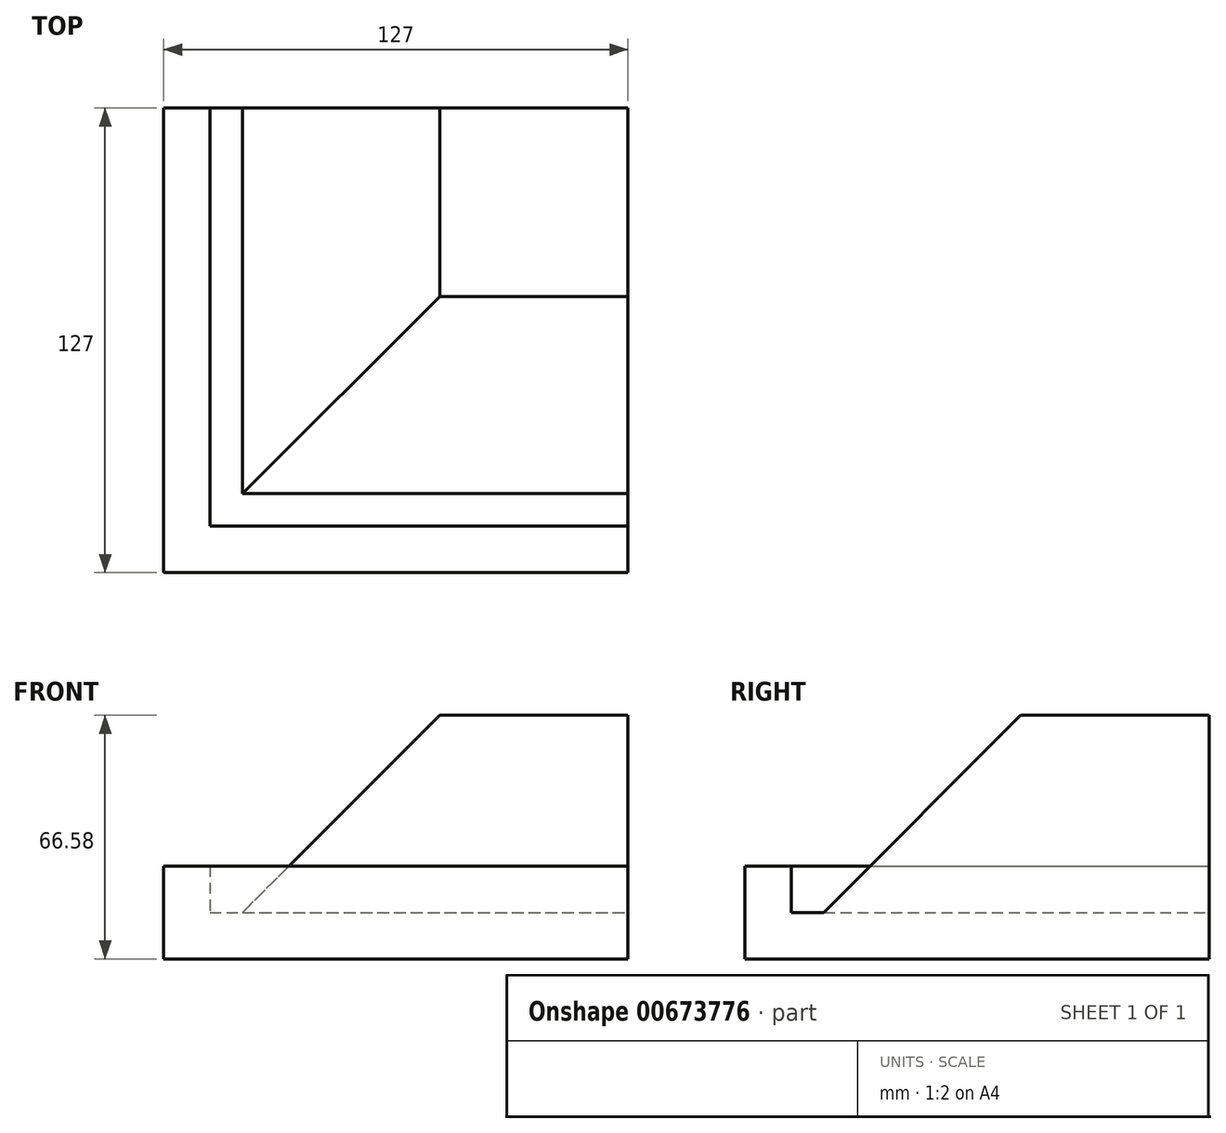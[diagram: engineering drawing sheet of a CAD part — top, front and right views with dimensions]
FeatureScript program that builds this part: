
annotation { "Feature Type Name" : "Feature", "Feature Type Description" : "" }
export const myFeature = defineFeature(function(context is Context, id is Id, definition is map)
    precondition{}
    {
        {
            var Q0;
            Q0=qCreatedBy(makeId("Top.planeOp"),FACE);
            var sketch = newSketch(context, id + "F0", { "sketchPlane" : qUnion([Q0])});
            skLineSegment(sketch, "E0.bottom", {"start": v(88.9, 88.9) * mm, "end": v(-88.9, 88.9) * mm});
            skLineSegment(sketch, "E0.top", {"start": v(88.9, -88.9) * mm, "end": v(-88.9, -88.9) * mm});
            skLineSegment(sketch, "E0.left", {"start": v(88.9, 88.9) * mm, "end": v(88.9, -88.9) * mm});
            skLineSegment(sketch, "E0.right", {"start": v(-88.9, 88.9) * mm, "end": v(-88.9, -88.9) * mm});
            skPoint(sketch, "E0.middle", {"position": v(0, 0) * mm});
            skSolve(sketch);
        }
        {
            var Q0;
            Q0 = qSketchRegion(id + "F0", true);
            extrude(context, id + "F1", {"entities" : qUnion([Q0]), "depth" : 76.2 * mm, "offsetDistance" : 25.4 * mm});
        }
        {
            var Q0;
            Q0=makeQuery(id+"F1.opExtrude","SWEPT_FACE",FACE,{"disambiguationData":[OSD([sQuery(id+"F0.wireOp",EDGE,"E0.bottom")])]});
            var sketch = newSketch(context, id + "F2", { "sketchPlane" : qUnion([Q0])});
            skLineSegment(sketch, "E1", {"start": v(88.9, 25.4) * mm, "end": v(76.2, 25.4) * mm});
            skLineSegment(sketch, "E2", {"start": v(76.2, 25.4) * mm, "end": v(76.2, 12.7) * mm});
            skLineSegment(sketch, "E3", {"start": v(76.2, 12.7) * mm, "end": v(67.31, 12.7) * mm});
            skLineSegment(sketch, "E4", {"start": v(67.31, 12.7) * mm, "end": v(13.43, 66.58) * mm});
            skLineSegment(sketch, "E5.0", {"start": v(-88.9, 0) * mm, "end": v(88.9, 0) * mm});
            skLineSegment(sketch, "E6", {"start": v(13.43, 66.58) * mm, "end": v(-11.97, 66.58) * mm});
            skLineSegment(sketch, "E7", {"start": v(-11.97, 66.58) * mm, "end": v(-11.97, 0) * mm});
            skLineSegment(sketch, "E8", {"start": v(-11.97, 66.58) * mm, "end": v(-11.97, 76.2) * mm});
            skLineSegment(sketch, "E9", {"start": v(-38.1, 0) * mm, "end": v(-38.1, 76.2) * mm});
            skSolve(sketch);
        }
        {
            var Q0;
            {var subQ5=sQuery(id+"F2.wireOp",EDGE,"E1");Q0=makeQuery(id+"F2.imprint","IMPRINT",FACE,{"disambiguationData":[TD([[makeQuery(id+"F2.imprint","IMPRINT",EDGE,{"derivedFrom":subQ5}),-1.0]])]});}
            extrude(context, id + "F3", {"entities" : qUnion([Q0]), "operationType" : NewBodyOperationType.REMOVE, "oppositeDirection" : true, "depth" : 156.21 * mm, "offsetDistance" : 25.4 * mm});
        }
        {
            var Q0;
            Q0=makeQuery(id+"F1.opExtrude","SWEPT_FACE",FACE,{"disambiguationData":[OSD([sQuery(id+"F0.wireOp",EDGE,"E0.left")])]});
            var sketch = newSketch(context, id + "F4", { "sketchPlane" : qUnion([Q0])});
            skLineSegment(sketch, "E10.0", {"start": v(88.9, 0) * mm, "end": v(-88.9, 0) * mm});
            skLineSegment(sketch, "E10.1", {"start": v(-88.9, 76.2) * mm, "end": v(-88.9, 0) * mm});
            skLineSegment(sketch, "E11", {"start": v(-88.9, 25.4) * mm, "end": v(-76.2, 25.4) * mm});
            skLineSegment(sketch, "E12", {"start": v(-76.2, 25.4) * mm, "end": v(-76.2, 12.7) * mm});
            skLineSegment(sketch, "E13", {"start": v(-76.2, 12.7) * mm, "end": v(-67.31, 12.7) * mm});
            skLineSegment(sketch, "E14", {"start": v(-67.31, 12.7) * mm, "end": v(-13.43, 66.58) * mm});
            skLineSegment(sketch, "E15", {"start": v(-13.43, 66.58) * mm, "end": v(11.97, 66.58) * mm});
            skLineSegment(sketch, "E16", {"start": v(11.97, 66.58) * mm, "end": v(11.97, 0) * mm});
            skLineSegment(sketch, "E17", {"start": v(11.97, 66.58) * mm, "end": v(11.97, 76.2) * mm});
            skLineSegment(sketch, "E18", {"start": v(38.1, 76.2) * mm, "end": v(38.1, 0) * mm});
            skSolve(sketch);
        }
        {
            var Q0;
            {var subQ0=sQuery(id+"F4.wireOp",EDGE,"E11");Q0=makeQuery(id+"F4.imprint","IMPRINT",FACE,{"disambiguationData":[TD([[makeQuery(id+"F4.imprint","IMPRINT",EDGE,{"derivedFrom":subQ0}),1.0]])]});}
            extrude(context, id + "F5", {"entities" : qUnion([Q0]), "operationType" : NewBodyOperationType.REMOVE, "oppositeDirection" : true, "depth" : 156.21 * mm, "offsetDistance" : 25.4 * mm});
        }
        {
            var Q0;
            Q0=makeQuery(id+"F5.boolean.opBoolean","COPY",FACE,{"derivedFrom":makeQuery(id+"F5.opExtrude","SWEPT_FACE",FACE,{"disambiguationData":[OSD([sQuery(id+"F4.wireOp",EDGE,"E17")])]})});
            extrude(context, id + "F6", {"entities" : qUnion([Q0]), "operationType" : NewBodyOperationType.REMOVE, "endBound" : BoundingType.THROUGH_ALL, "oppositeDirection" : true, "depth" : 25.4 * mm, "offsetDistance" : 25.4 * mm});
        }
        {
            var Q0;
            Q0=makeQuery(id+"F5.boolean.opBoolean","COPY",FACE,{"derivedFrom":makeQuery(id+"F5.opExtrude","CAP_FACE",FACE,{"disambiguationData":[OSD([sQuery(id+"F0.wireOp",EDGE,"E0.left"),sQuery(id+"F4.wireOp",EDGE,"E10.1"),sQuery(id+"F4.wireOp",EDGE,"E11"),sQuery(id+"F4.wireOp",EDGE,"E12"),sQuery(id+"F4.wireOp",EDGE,"E13"),sQuery(id+"F4.wireOp",EDGE,"E14"),sQuery(id+"F4.wireOp",EDGE,"E15"),sQuery(id+"F4.wireOp",EDGE,"E17")])],"isStart":false})});
            var sketch = newSketch(context, id + "F7", { "sketchPlane" : qUnion([Q0])});
            skLineSegment(sketch, "E19.0", {"start": v(-88.9, 25.4) * mm, "end": v(-76.2, 25.4) * mm});
            skLineSegment(sketch, "E20", {"start": v(-76.2, 25.4) * mm, "end": v(-67.31, 25.4) * mm});
            skSolve(sketch);
        }
        {
            var Q0;
            Q0 = qSketchRegion(id + "F7", true);
            var Q1;
            Q1=makeQuery(id+"F7.imprint","IMPRINT",FACE,{"disambiguationData":[TD([[makeQuery(id+"F7.imprint","IMPRINT",EDGE,{"derivedFrom":sQuery(id+"F7.wireOp",EDGE,"E19.0")}),1.0]])]});
            extrude(context, id + "F8", {"entities" : qUnion([Q0, Q1]), "operationType" : NewBodyOperationType.REMOVE, "endBound" : BoundingType.THROUGH_ALL, "oppositeDirection" : true, "depth" : 25.4 * mm, "offsetDistance" : 25.4 * mm});
        }
        {
            var Q0;
            Q0=makeQuery(id+"F5.boolean.opBoolean","COPY",FACE,{"derivedFrom":makeQuery(id+"F5.opExtrude","CAP_FACE",FACE,{"disambiguationData":[OSD([sQuery(id+"F0.wireOp",EDGE,"E0.left"),sQuery(id+"F4.wireOp",EDGE,"E10.1"),sQuery(id+"F4.wireOp",EDGE,"E11"),sQuery(id+"F4.wireOp",EDGE,"E12"),sQuery(id+"F4.wireOp",EDGE,"E13"),sQuery(id+"F4.wireOp",EDGE,"E14"),sQuery(id+"F4.wireOp",EDGE,"E15"),sQuery(id+"F4.wireOp",EDGE,"E17")])],"isStart":false})});
            extrude(context, id + "F9", {"entities" : qUnion([Q0]), "operationType" : NewBodyOperationType.REMOVE, "oppositeDirection" : true, "depth" : 8.9 * mm, "offsetDistance" : 25.4 * mm});
        }
        {
            var Q0;
            {var subQ3=sQuery(id+"F2.wireOp",EDGE,"E9");Q0=makeQuery(id+"F2.imprint","IMPRINT",FACE,{"disambiguationData":[TD([[makeQuery(id+"F2.imprint","IMPRINT",EDGE,{"derivedFrom":subQ3}),1.0]])]});}
            extrude(context, id + "F10", {"entities" : qUnion([Q0]), "operationType" : NewBodyOperationType.REMOVE, "endBound" : BoundingType.THROUGH_ALL, "oppositeDirection" : true, "depth" : 25.4 * mm, "offsetDistance" : 25.4 * mm});
        }
        {
            var Q0;
            {var subQ3=sQuery(id+"F4.wireOp",EDGE,"E18");Q0=makeQuery(id+"F4.imprint","IMPRINT",FACE,{"disambiguationData":[TD([[makeQuery(id+"F4.imprint","IMPRINT",EDGE,{"derivedFrom":subQ3}),1.0]])]});}
            extrude(context, id + "F11", {"entities" : qUnion([Q0]), "operationType" : NewBodyOperationType.REMOVE, "endBound" : BoundingType.THROUGH_ALL, "oppositeDirection" : true, "depth" : 25.4 * mm, "offsetDistance" : 25.4 * mm});
        }
    });
